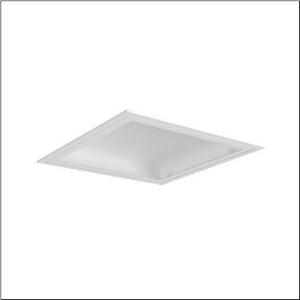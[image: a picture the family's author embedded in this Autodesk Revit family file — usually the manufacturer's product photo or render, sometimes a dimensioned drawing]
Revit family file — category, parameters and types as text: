
# Revit family: mira_r__21_51fr427a432a_cde4
name_source: partatom
category: Lighting Fixtures
units: mm (PartAtom-declared; Revit-internal decimal feet)

## family parameters
Cut with Voids When Loaded = No
Host = Face
Light Source = No
Part Type = Normal
Room Calculation Point = No
Round Connector Dimension = Use Diameter
Shared = No

## types (1)
- Mira® 21 (1 x LED, 3220 lm, 23 W, 4000K)
    Apparent Load = 23 VA
    CIE Flux Codes = 50 81 97 100 100
    Color Rendering = 80
    Color Temperature = 4000K
    Default Elevation = 1800 mm
    Description = Mira® 21, clean room luminaire, primary light control with reflector, primary optical cover: cover, of PC, light emission: direct distribution, primary light characteristic: symmetric, installation type: recessed, LED, rated luminous flux: 3.220lm, luminous efficacy: 140lm/W, light colour: 840, colour temperature: 4000K, control gear: ECG, with terminal, 3-pole, max. 2.5mm², mains connection: 230V, AC, 50/60Hz, rated input power: 23W, luminaire housing, of sheet steel, coated, pure white, module: M625, length: 623mm, width: 623mm, height: 115mm, protection rating (complete): IP54, insulation class (complete): insulation class I (protective earthing), certification: CE, UKCA, permissible operating ambient temperature: -5..+40°C, standard: EN 50419, packaging unit: 1 piece
    Height = 0 mm  [stored 0 ft]
    Lamp = 1 x LED
    Lamp Light Flux = 3220 lm
    Lamp Power = 23 W
    Lamp count = 1
    Length = 625 mm
    Luminous efficacy = 140 lm/W
    Manufacturer = Siteco
    ModVariant = No
    Model = 51FR427A432A
    Mounting Place = Ceiling
    Mounting Type = Recessed
    Number of Poles = 1
    OnlyDefault = Yes
    Power Factor = 1
    Product Name = Mira® 21
    Product group = clean room luminaire
    ProductGroupID = 401
    Protection Class = Protection class I
    Protection Degree = IP 54
    RLX_Detail_Level = 1
    RlxData = <blob elided: 13309 chars, md5=683fb0ac>
    Socket = socket
    Standby Power = 0 W
    System Light Flux = 3220 lm
    System Power = 23 W
    Type Comments = Product without accessories
    Type Image = l_1007109.jpg
    URL = http://relux.com
    VarID = ---
    Voltage = 0 V
    Weight = 0.00 kg
    Width = 625 mm

note: [stored X ft] marks values corroborated as IEEE doubles in the binary element streams (Revit-internal decimal feet)

## geometry (parser evidence)
native form markers: Sweep x7
no freeform markers — native parametric forms only
